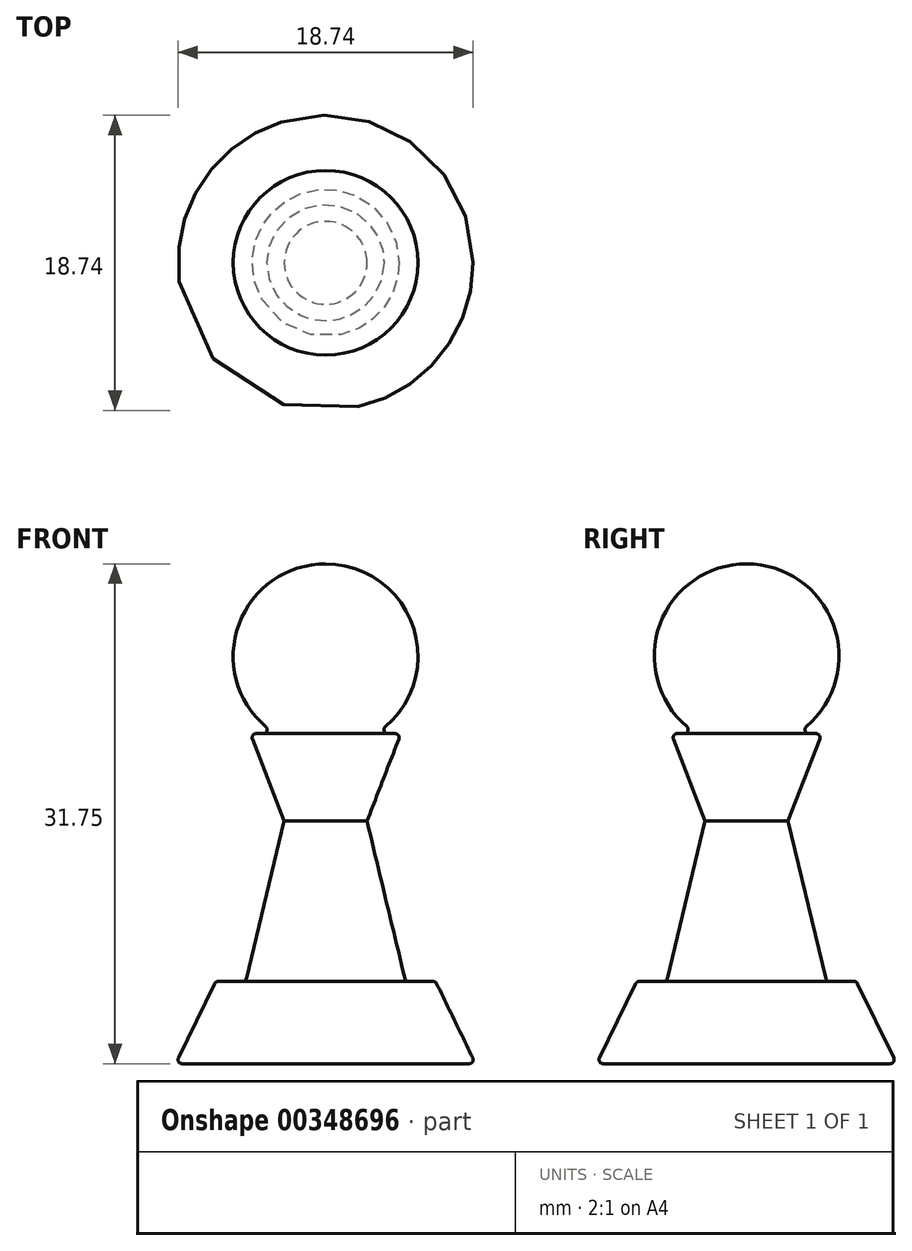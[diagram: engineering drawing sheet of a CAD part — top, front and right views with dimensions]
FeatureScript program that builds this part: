
annotation { "Feature Type Name" : "Feature", "Feature Type Description" : "" }
export const myFeature = defineFeature(function(context is Context, id is Id, definition is map)
    precondition{}
    {
        {
            var Q0;
            Q0=qCreatedBy(makeId("Front.planeOp"),FACE);
            var sketch = newSketch(context, id + "F0", { "sketchPlane" : qUnion([Q0])});
            skLineSegment(sketch, "E0.bottom", {"start": v(9.53, -31.75) * mm, "end": v(-9.52, -31.75) * mm, "construction": true});
            skLineSegment(sketch, "E0.top", {"start": v(9.52, 31.75) * mm, "end": v(-9.53, 31.75) * mm, "construction": true});
            skLineSegment(sketch, "E0.left", {"start": v(9.53, -31.75) * mm, "end": v(9.52, 31.75) * mm, "construction": true});
            skLineSegment(sketch, "E0.right", {"start": v(-9.52, -31.75) * mm, "end": v(-9.53, 31.75) * mm, "construction": true});
            skPoint(sketch, "E0.middle", {"position": v(0, 0) * mm});
            skLineSegment(sketch, "E1", {"start": v(-9.53, 0) * mm, "end": v(9.53, 0) * mm, "construction": true});
            skArc(sketch, "E2", {"start": v(0, 31.75) * mm, "mid": v(-5.5, 27.9) * mm, "end": v(-3.8, 21.41) * mm});
            skLineSegment(sketch, "E3", {"start": v(0, 0) * mm, "end": v(-9.12, 0) * mm});
            skLineSegment(sketch, "E4", {"start": v(-9.35, 0.37) * mm, "end": v(-7.05, 5.08) * mm});
            skLineSegment(sketch, "E5", {"start": v(-6.82, 5.22) * mm, "end": v(-5.28, 5.22) * mm});
            skLineSegment(sketch, "E6", {"start": v(0, 5.22) * mm, "end": v(0, 0) * mm});
            skLineSegment(sketch, "E7", {"start": v(-5.03, 5.42) * mm, "end": v(-2.63, 15.4) * mm});
            skLineSegment(sketch, "E8", {"start": v(-2.63, 15.4) * mm, "end": v(-4.65, 20.62) * mm});
            skLineSegment(sketch, "E9", {"start": v(0, 5.22) * mm, "end": v(0, 20.02) * mm});
            skLineSegment(sketch, "E10", {"start": v(-4.41, 20.97) * mm, "end": v(-3.96, 20.97) * mm});
            skLineSegment(sketch, "E11", {"start": v(0, 31.75) * mm, "end": v(0, 20.02) * mm});
            skPoint(sketch, "E12.orphan", {"position": v(0, 20.97) * mm});
            skPoint(sketch, "E13.visualSharp", {"position": v(-3.2, 20.97) * mm});
            skArc(sketch, "E13.filletArc", {"start": v(-3.96, 20.97) * mm, "mid": v(-3.73, 21.13) * mm, "end": v(-3.8, 21.41) * mm});
            skPoint(sketch, "E14.visualSharp", {"position": v(-4.78, 20.97) * mm});
            skArc(sketch, "E14.filletArc", {"start": v(-4.41, 20.97) * mm, "mid": v(-4.62, 20.86) * mm, "end": v(-4.65, 20.62) * mm});
            skPoint(sketch, "E15.visualSharp", {"position": v(-9.53, 0) * mm});
            skArc(sketch, "E15.filletArc", {"start": v(-9.35, 0.37) * mm, "mid": v(-9.33, 0.12) * mm, "end": v(-9.12, 0) * mm});
            skPoint(sketch, "E16.visualSharp", {"position": v(-5.08, 5.22) * mm});
            skArc(sketch, "E16.filletArc", {"start": v(-5.28, 5.22) * mm, "mid": v(-5.12, 5.28) * mm, "end": v(-5.03, 5.42) * mm});
            skPoint(sketch, "E17.visualSharp", {"position": v(-6.98, 5.22) * mm});
            skArc(sketch, "E17.filletArc", {"start": v(-6.82, 5.22) * mm, "mid": v(-6.96, 5.19) * mm, "end": v(-7.05, 5.08) * mm});
            skSolve(sketch);
        }
        {
            var Q0;
            Q0 = qSketchRegion(id + "F0", true);
            var Q1;
            Q1=sQuery(id+"F0.wireOp",EDGE,"E11");
            revolve(context, id + "F1", {"entities" : qUnion([Q0]), "axis" : qUnion([Q1]), "revolveType" : RevolveType.FULL});
        }
    });
